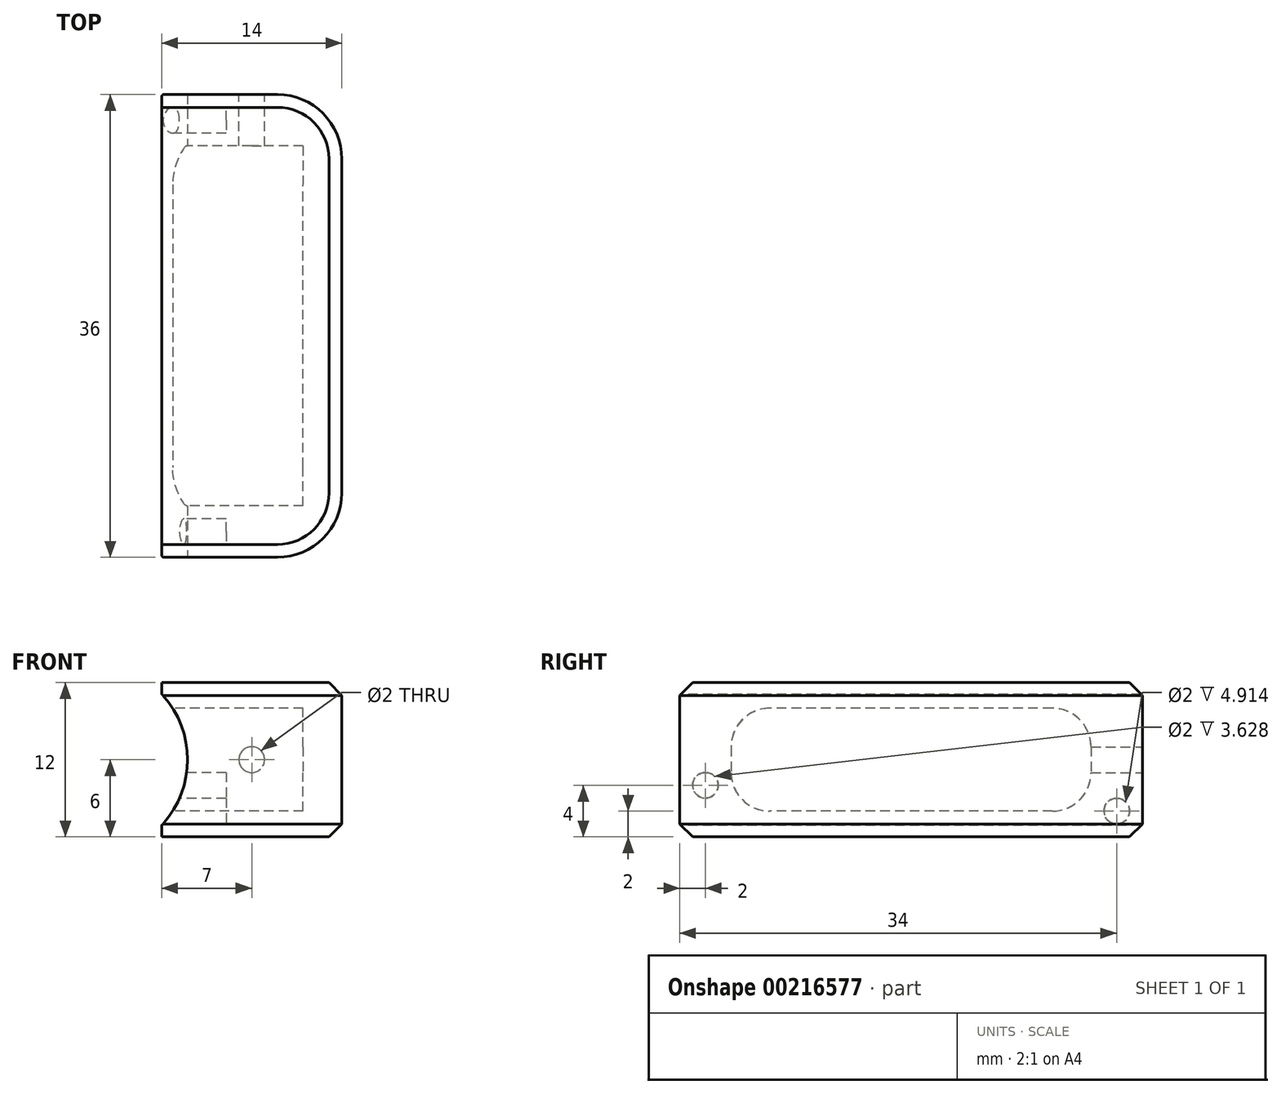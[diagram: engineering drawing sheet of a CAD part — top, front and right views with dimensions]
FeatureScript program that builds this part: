
annotation { "Feature Type Name" : "Feature", "Feature Type Description" : "" }
export const myFeature = defineFeature(function(context is Context, id is Id, definition is map)
    precondition{}
    {
        {
            var Q0;
            Q0=qCreatedBy(makeId("Top.planeOp"),FACE);
            var sketch = newSketch(context, id + "F0", { "sketchPlane" : qUnion([Q0])});
            skLineSegment(sketch, "E0.bottom", {"start": v(-7, 18) * mm, "end": v(7, 18) * mm});
            skLineSegment(sketch, "E0.top", {"start": v(-7, -18) * mm, "end": v(7, -18) * mm});
            skLineSegment(sketch, "E0.left", {"start": v(-7, 18) * mm, "end": v(-7, -18) * mm});
            skLineSegment(sketch, "E0.right", {"start": v(7, 18) * mm, "end": v(7, -18) * mm});
            skSolve(sketch);
        }
        {
            var Q0;
            Q0 = qSketchRegion(id + "F0", true);
            extrude(context, id + "F1", {"entities" : qUnion([Q0]), "depth" : 12 * mm});
        }
        {
            var Q0;
            Q0=makeQuery(id+"F1.opExtrude","SWEPT_FACE",FACE,{"disambiguationData":[OSD([sQuery(id+"F0.wireOp",EDGE,"E0.top")])]});
            var sketch = newSketch(context, id + "F2", { "sketchPlane" : qUnion([Q0])});
            skCircle(sketch, "E1", {"center": v(-12.5, 6) * mm, "radius": 7.5 * mm});
            skSolve(sketch);
        }
        {
            var Q0;
            Q0 = qSketchRegion(id + "F2", true);
            extrude(context, id + "F3", {"entities" : qUnion([Q0]), "operationType" : NewBodyOperationType.REMOVE, "endBound" : BoundingType.THROUGH_ALL, "oppositeDirection" : true, "depth" : 25 * mm});
        }
        {
            var Q0;
            Q0=qCreatedBy(makeId("Right.planeOp"),FACE);
            cPlane(context, id + "F4", {"entities" : qUnion([Q0]), "cplaneType" : CPlaneType.OFFSET, "offset" : 7 * mm, "oppositeDirection" : true, "width" : 150 * mm, "height" : 150 * mm});
        }
        {
            var Q0;
            Q0=qCreatedBy(id+"F4.planeOp",FACE);
            var sketch = newSketch(context, id + "F5", { "sketchPlane" : qUnion([Q0])});
            skLineSegment(sketch, "E2.bottom", {"start": v(-14, 10) * mm, "end": v(14, 10) * mm});
            skLineSegment(sketch, "E2.top", {"start": v(-14, 2) * mm, "end": v(14, 2) * mm});
            skLineSegment(sketch, "E2.left", {"start": v(-14, 10) * mm, "end": v(-14, 2) * mm});
            skLineSegment(sketch, "E2.right", {"start": v(14, 10) * mm, "end": v(14, 2) * mm});
            skSolve(sketch);
        }
        {
            var Q0;
            Q0 = qSketchRegion(id + "F5", true);
            extrude(context, id + "F6", {"entities" : qUnion([Q0]), "operationType" : NewBodyOperationType.REMOVE, "depth" : 11 * mm});
        }
        {
            var Q0;
            Q0=makeQuery(id+"F6.boolean.opBoolean","COPY",EDGE,{"derivedFrom":makeQuery(id+"F6.opExtrude","SWEPT_EDGE",EDGE,{"disambiguationData":[OSD([sQuery(id+"F5.wireOp",EDGE,"E2.top"),sQuery(id+"F5.wireOp",EDGE,"E2.right")])]})});
            var Q1;
            Q1=makeQuery(id+"F6.boolean.opBoolean","COPY",EDGE,{"derivedFrom":makeQuery(id+"F6.opExtrude","SWEPT_EDGE",EDGE,{"disambiguationData":[OSD([sQuery(id+"F5.wireOp",EDGE,"E2.bottom"),sQuery(id+"F5.wireOp",EDGE,"E2.left")])]})});
            var Q2;
            Q2=makeQuery(id+"F6.boolean.opBoolean","COPY",EDGE,{"derivedFrom":makeQuery(id+"F6.opExtrude","SWEPT_EDGE",EDGE,{"disambiguationData":[OSD([sQuery(id+"F5.wireOp",EDGE,"E2.top"),sQuery(id+"F5.wireOp",EDGE,"E2.left")])]})});
            var Q3;
            Q3=makeQuery(id+"F6.boolean.opBoolean","COPY",EDGE,{"derivedFrom":makeQuery(id+"F6.opExtrude","SWEPT_EDGE",EDGE,{"disambiguationData":[OSD([sQuery(id+"F5.wireOp",EDGE,"E2.bottom"),sQuery(id+"F5.wireOp",EDGE,"E2.right")])]})});
            fillet(context, id + "F7", {"entities" : qUnion([Q0, Q1, Q2, Q3]), "radius" : 3 * mm, "tangentPropagation" : true, "allowEdgeOverflow" : false});
        }
        {
            var Q0;
            Q0=makeQuery(id+"F1.opExtrude","SWEPT_EDGE",EDGE,{"disambiguationData":[OSD([sQuery(id+"F0.wireOp",EDGE,"E0.top"),sQuery(id+"F0.wireOp",EDGE,"E0.right")])]});
            var Q1;
            Q1=makeQuery(id+"F1.opExtrude","SWEPT_EDGE",EDGE,{"disambiguationData":[OSD([sQuery(id+"F0.wireOp",EDGE,"E0.bottom"),sQuery(id+"F0.wireOp",EDGE,"E0.right")])]});
            fillet(context, id + "F8", {"entities" : qUnion([Q0, Q1]), "radius" : 5 * mm, "tangentPropagation" : true, "allowEdgeOverflow" : false});
        }
        {
            var Q0;
            Q0=makeQuery(id+"F1.opExtrude","CAP_EDGE",EDGE,{"disambiguationData":[OSD([sQuery(id+"F0.wireOp",EDGE,"E0.top")])],"isStart":true});
            var Q1;
            Q1=makeQuery(id+"F1.opExtrude","CAP_EDGE",EDGE,{"disambiguationData":[OSD([sQuery(id+"F0.wireOp",EDGE,"E0.top")])],"isStart":false});
            chamfer(context, id + "F9", {"entities" : qUnion([Q0, Q1]), "width" : 1 * mm, "tangentPropagation" : true});
        }
        {
            var Q0;
            Q0=makeQuery(id+"F1.opExtrude","SWEPT_FACE",FACE,{"disambiguationData":[OSD([sQuery(id+"F0.wireOp",EDGE,"E0.bottom")])]});
            var sketch = newSketch(context, id + "F10", { "sketchPlane" : qUnion([Q0])});
            skCircle(sketch, "E3", {"center": v(0, 6) * mm, "radius": 1 * mm});
            skSolve(sketch);
        }
        {
            var Q0;
            Q0 = qSketchRegion(id + "F10", true);
            extrude(context, id + "F11", {"entities" : qUnion([Q0]), "operationType" : NewBodyOperationType.REMOVE, "endBound" : BoundingType.UP_TO_NEXT, "oppositeDirection" : true, "depth" : 25 * mm});
        }
        {
            var Q0;
            Q0=qCreatedBy(id+"F4.planeOp",FACE);
            var sketch = newSketch(context, id + "F12", { "sketchPlane" : qUnion([Q0])});
            skCircle(sketch, "E4", {"center": v(-16, 4) * mm, "radius": 1 * mm});
            skCircle(sketch, "E5", {"center": v(16, 2) * mm, "radius": 1 * mm});
            skSolve(sketch);
        }
        {
            var Q0;
            Q0 = qSketchRegion(id + "F12", true);
            extrude(context, id + "F13", {"entities" : qUnion([Q0]), "operationType" : NewBodyOperationType.REMOVE, "depth" : 5 * mm});
        }
    });
